# Revit family: NNYC2001188
name_source: partatom
category: 照明器具
revit_build: Autodesk Revit 2018 (Build: 20170223_1515(x64)
units: mm (PartAtom-declared; Revit-internal decimal feet)

## family parameters
OmniClass タイトル = Lighting
OmniClass 番号 = 23.80.70.00
パーツ タイプ = 標準
ロード時にボイドで切り取り = いいえ
丸型コネクタ寸法 = 直径を使用
作業面ベース = はい
光源 = はい
共有 = いいえ
常に垂直 = いいえ
部屋計算ポイント = いいえ

## types (1)
- NNYC2001188
    Body = ADC12
    Height = 0  [stored 0 ft]
    Length = 0  [stored 0 ft]
    Light Source = Light Source
    URL = https://panasonic.net
    Voltage = 230 V
    Width = 0  [stored 0 ft]
    カラー フィルタ = 16777215
    タイプのイメージ = <なし>
    タイプの説明 = Street Light
    フォトメトリック Web ファイル = NNYC2001188.ies
    モデル = LED Street Light SP series
    レンダリング時に放射形状を表示 = いいえ
    価格 = 0 $
    傾斜角 = 90.00°
    既定の高さ = 0  [stored 0 ft]
    製造元 = Panasonic Corp.
    説明 = NNYC2001188
    調光ランプの色温度変化。 = <なし>
    長方形の幅に沿って放射 = 154  [stored 0.505249 ft]
    長方形の長さに沿って放射 = 52

note: [stored X ft] marks values corroborated as IEEE doubles in the binary element streams (Revit-internal decimal feet)

## geometry (parser evidence)
native form markers: Sweep x1
no freeform markers — native parametric forms only
